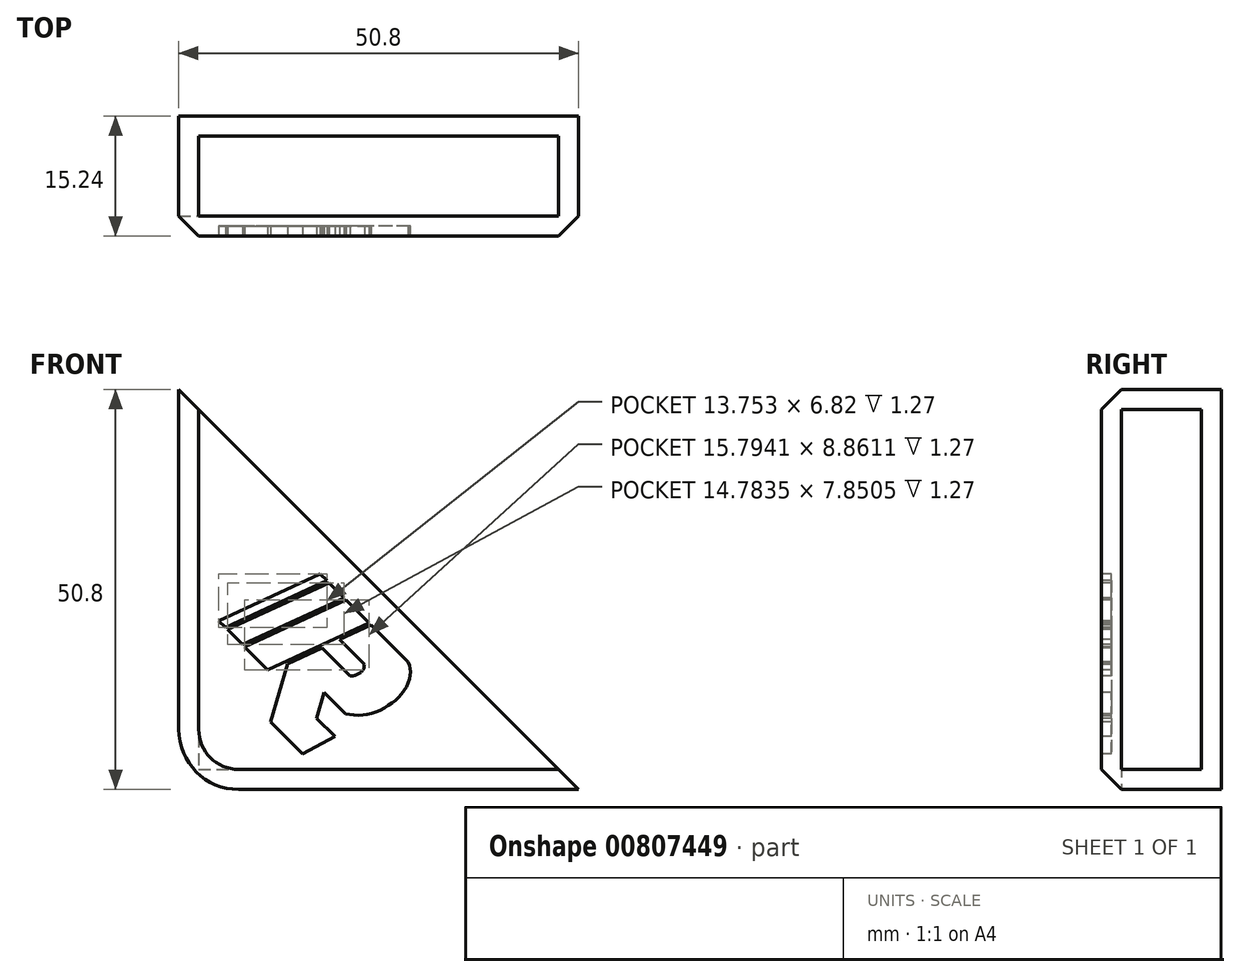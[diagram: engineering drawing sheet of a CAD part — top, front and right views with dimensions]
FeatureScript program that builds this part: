
annotation { "Feature Type Name" : "Feature", "Feature Type Description" : "" }
export const myFeature = defineFeature(function(context is Context, id is Id, definition is map)
    precondition{}
    {
        {
            var Q0;
            Q0=qCreatedBy(makeId("Front.planeOp"),FACE);
            var sketch = newSketch(context, id + "F0", { "sketchPlane" : qUnion([Q0])});
            skLineSegment(sketch, "E0", {"start": v(-25.3, 27.1) * mm, "end": v(-25.3, -23.7) * mm});
            skLineSegment(sketch, "E1", {"start": v(-25.3, -23.7) * mm, "end": v(25.5, -23.7) * mm});
            skLineSegment(sketch, "E2", {"start": v(25.5, -23.7) * mm, "end": v(-25.3, 27.1) * mm});
            skSolve(sketch);
        }
        {
            var Q0;
            Q0 = qSketchRegion(id + "F0", true);
            extrude(context, id + "F1", {"entities" : qUnion([Q0]), "depth" : 15.24 * mm, "offsetDistance" : 25.4 * mm});
        }
        {
            var Q0;
            Q0=makeQuery(id+"F1.opExtrude","SWEPT_FACE",FACE,{"disambiguationData":[OSD([sQuery(id+"F0.wireOp",EDGE,"E2")])]});
            shell(context, id + "F2", {"entities" : qUnion([Q0]), "thickness" : 2.54 * mm});
        }
        {
            var Q0;
            Q0=makeQuery(id+"F1.opExtrude","CAP_FACE",FACE,{"disambiguationData":[OSD([sQuery(id+"F0.wireOp",EDGE,"E0"),sQuery(id+"F0.wireOp",EDGE,"E1"),sQuery(id+"F0.wireOp",EDGE,"E2")])],"isStart":false});
            var sketch = newSketch(context, id + "F3", { "sketchPlane" : qUnion([Q0])});
            skLineSegment(sketch, "E3", {"start": v(-20.23, -2.28) * mm, "end": v(-7.34, 3.68) * mm});
            skLineSegment(sketch, "E4", {"start": v(-14, -8.5) * mm, "end": v(-16.9, -5.6) * mm});
            skLineSegment(sketch, "E5", {"start": v(-6.47, 2.81) * mm, "end": v(-19.36, -3.14) * mm});
            skLineSegment(sketch, "E6", {"start": v(-19.1, -3.41) * mm, "end": v(-6.2, 2.54) * mm});
            skLineSegment(sketch, "E7", {"start": v(-4.3, 0.65) * mm, "end": v(-17.2, -5.3) * mm});
            skLineSegment(sketch, "E8", {"start": v(-16.9, -5.6) * mm, "end": v(-4.02, 0.36) * mm});
            skLineSegment(sketch, "E9", {"start": v(-1.11, -2.55) * mm, "end": v(-14, -8.5) * mm});
            skLineSegment(sketch, "E10", {"start": v(-4.87, -4.67) * mm, "end": v(-0.85, -2.8) * mm});
            skLineSegment(sketch, "E11", {"start": v(-4.87, -4.67) * mm, "end": v(-1.72, -7.82) * mm});
            skLineSegment(sketch, "E12", {"start": v(-3.54, -9.3) * mm, "end": v(-7.1, -5.74) * mm});
            skLineSegment(sketch, "E13", {"start": v(-7.1, -5.74) * mm, "end": v(-11.48, -7.77) * mm});
            skLineSegment(sketch, "E14", {"start": v(-11.48, -7.77) * mm, "end": v(-13.66, -15.15) * mm});
            skLineSegment(sketch, "E15", {"start": v(-13.66, -15.15) * mm, "end": v(-9.59, -19.22) * mm});
            skLineSegment(sketch, "E16", {"start": v(-9.59, -19.22) * mm, "end": v(-5.45, -17) * mm});
            skLineSegment(sketch, "E17", {"start": v(-5.45, -17) * mm, "end": v(-7.8, -14.66) * mm});
            skLineSegment(sketch, "E18", {"start": v(-7.8, -14.66) * mm, "end": v(-6.84, -11.39) * mm});
            skLineSegment(sketch, "E19", {"start": v(-6.84, -11.39) * mm, "end": v(-4.12, -14.1) * mm});
            skFitSpline(sketch, "E20", {"points": [v(3.86, -7.52) * mm, v(4.14, -8.66) * mm, v(3.92, -9.94) * mm, v(3.04, -11.57) * mm, v(1.61, -12.85) * mm, v(-0.25, -13.9) * mm, v(-2.24, -14.29) * mm, v(-4.12, -14.1) * mm], "startDerivative": vector(3.2, -9.64) * mm, "endDerivative": vector(-12.5, 1.99) * mm});
            skLineSegment(sketch, "E21.trimOffspring", {"start": v(-6.47, 2.81) * mm, "end": v(-7.34, 3.68) * mm});
            skLineSegment(sketch, "E22.trimOffspring", {"start": v(-4.3, 0.65) * mm, "end": v(-6.2, 2.54) * mm});
            skLineSegment(sketch, "E23.trimOffspring", {"start": v(-1.11, -2.55) * mm, "end": v(-4.02, 0.36) * mm});
            skLineSegment(sketch, "E24.trimOffspring", {"start": v(3.86, -7.52) * mm, "end": v(-0.85, -2.8) * mm});
            skLineSegment(sketch, "E25.trimOffspring", {"start": v(-17.2, -5.3) * mm, "end": v(-19.1, -3.41) * mm});
            skLineSegment(sketch, "E26.trimOffspring", {"start": v(-19.36, -3.14) * mm, "end": v(-20.23, -2.28) * mm});
            skFitSpline(sketch, "E27", {"points": [v(-1.72, -7.82) * mm, v(-1.84, -8.46) * mm, v(-2.4, -8.98) * mm, v(-3.2, -9.3) * mm, v(-3.54, -9.3) * mm], "startDerivative": vector(-0.16, -2.65) * mm, "endDerivative": vector(-1.62, 0.25) * mm});
            skLineSegment(sketch, "E28.0", {"start": v(-3.2, -9.3) * mm, "end": v(-1.72, -7.82) * mm, "construction": true});
            skSolve(sketch);
        }
        {
            var Q0;
            Q0 = qSketchRegion(id + "F3", true);
            extrude(context, id + "F4", {"entities" : qUnion([Q0]), "operationType" : NewBodyOperationType.REMOVE, "oppositeDirection" : true, "depth" : 1.27 * mm, "offsetDistance" : 25.4 * mm});
        }
        {
            var Q0;
            Q0=makeQuery(id+"F1.opExtrude","SWEPT_EDGE",EDGE,{"disambiguationData":[OSD([sQuery(id+"F0.wireOp",EDGE,"E0"),sQuery(id+"F0.wireOp",EDGE,"E1")])]});
            fillet(context, id + "F5", {"entities" : qUnion([Q0]), "radius" : 7.62 * mm, "tangentPropagation" : true, "allowEdgeOverflow" : false});
        }
        {
            var Q0;
            Q0=makeQuery(id+"F1.opExtrude","CAP_EDGE",EDGE,{"disambiguationData":[OSD([sQuery(id+"F0.wireOp",EDGE,"E0")])],"isStart":false});
            chamfer(context, id + "F6", {"entities" : qUnion([Q0]), "width" : 2.54 * mm, "tangentPropagation" : true});
        }
    });
